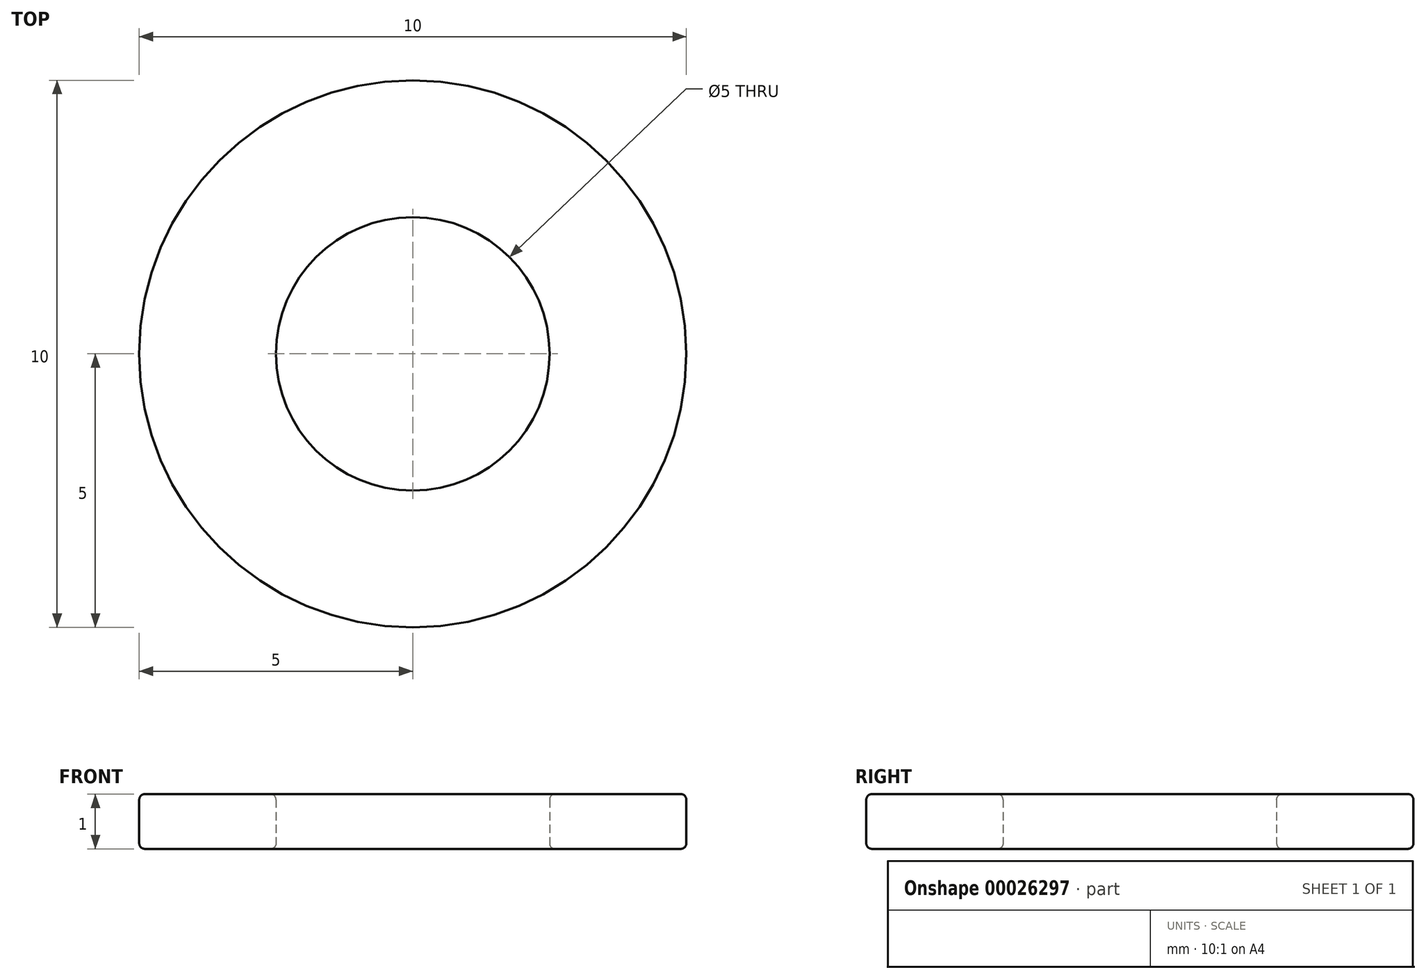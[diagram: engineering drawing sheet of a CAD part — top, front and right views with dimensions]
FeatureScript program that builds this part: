
annotation { "Feature Type Name" : "Feature", "Feature Type Description" : "" }
export const myFeature = defineFeature(function(context is Context, id is Id, definition is map)
    precondition{}
    {
        {
            var Q0;
            Q0=qCreatedBy(makeId("Top.planeOp"),FACE);
            var sketch = newSketch(context, id + "F0", { "sketchPlane" : qUnion([Q0])});
            skCircle(sketch, "E0", {"center": v(0, 0) * mm, "radius": 2.5 * mm});
            skCircle(sketch, "E1", {"center": v(0, 0) * mm, "radius": 5 * mm});
            skSolve(sketch);
        }
        {
            var Q0;
            Q0 = qSketchRegion(id + "F0", true);
            extrude(context, id + "F1", {"entities" : qUnion([Q0]), "depth" : 1 * mm});
        }
        {
            var Q0;
            Q0=makeQuery(id+"F1.opExtrude","CAP_EDGE",EDGE,{"disambiguationData":[OSD([sQuery(id+"F0.wireOp",EDGE,"E0")])],"isStart":false});
            var Q1;
            Q1=makeQuery(id+"F1.opExtrude","CAP_EDGE",EDGE,{"disambiguationData":[OSD([sQuery(id+"F0.wireOp",EDGE,"E0")])],"isStart":true});
            var Q2;
            Q2=makeQuery(id+"F1.opExtrude","CAP_EDGE",EDGE,{"disambiguationData":[OSD([sQuery(id+"F0.wireOp",EDGE,"E1")])],"isStart":true});
            var Q3;
            Q3=makeQuery(id+"F1.opExtrude","CAP_EDGE",EDGE,{"disambiguationData":[OSD([sQuery(id+"F0.wireOp",EDGE,"E1")])],"isStart":false});
            fillet(context, id + "F2", {"entities" : qUnion([Q0, Q1, Q2, Q3]), "radius" : .1 * mm, "tangentPropagation" : true, "allowEdgeOverflow" : false});
        }
    });
